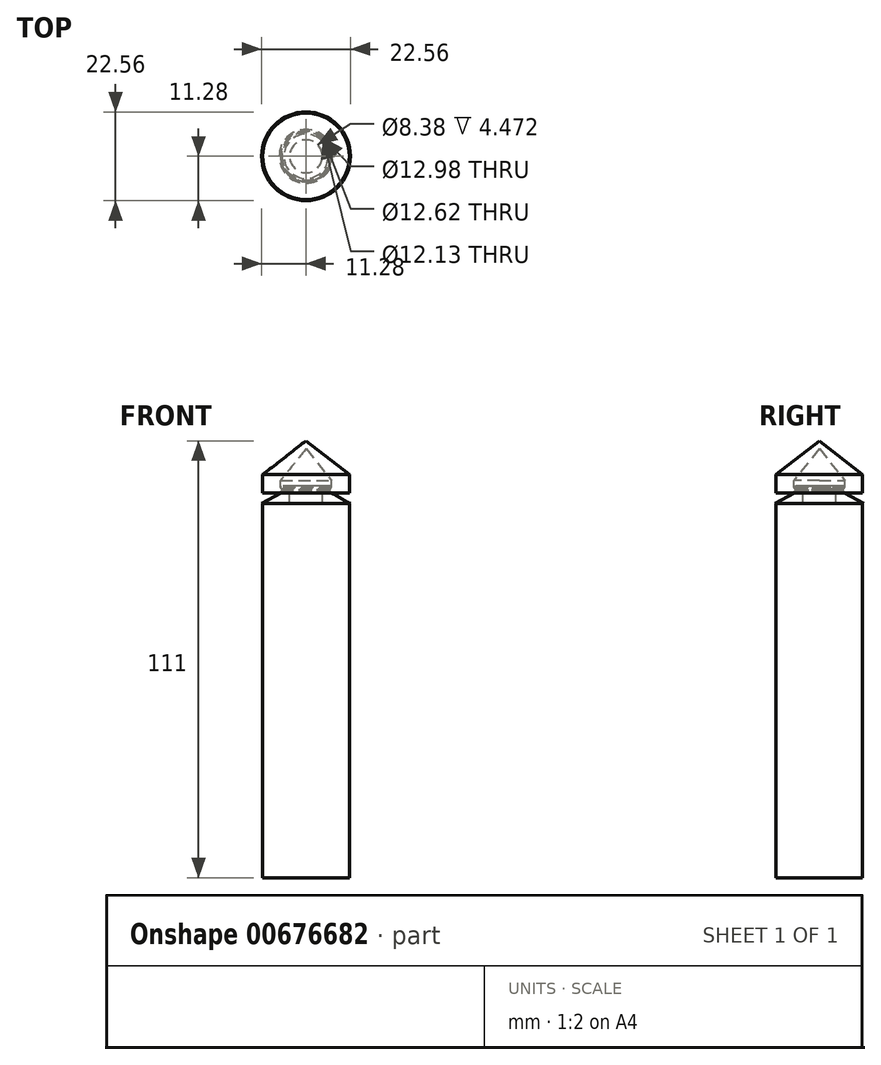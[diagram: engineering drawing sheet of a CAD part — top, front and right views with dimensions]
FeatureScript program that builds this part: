
annotation { "Feature Type Name" : "Feature", "Feature Type Description" : "" }
export const myFeature = defineFeature(function(context is Context, id is Id, definition is map)
    precondition{}
    {
        {
            var Q0;
            Q0=qCreatedBy(makeId("Front.planeOp"),FACE);
            var sketch = newSketch(context, id + "F0", { "sketchPlane" : qUnion([Q0])});
            skLineSegment(sketch, "E0", {"start": v(0, 27.08) * mm, "end": v(0, -28.09) * mm});
            skLineSegment(sketch, "E1", {"start": v(0, 21.5) * mm, "end": v(11, 12.9) * mm});
            skLineSegment(sketch, "E2", {"start": v(6.5, 11.4) * mm, "end": v(0, 19.49) * mm});
            skLineSegment(sketch, "E3", {"start": v(0, -89.5) * mm, "end": v(12.79, -89.5) * mm});
            skLineSegment(sketch, "E4", {"start": v(12.79, -89.5) * mm, "end": v(11, -89.5) * mm});
            skLineSegment(sketch, "E5", {"start": v(11, -89.5) * mm, "end": v(11, 5.52) * mm});
            skLineSegment(sketch, "E6", {"start": v(11.72, 5.52) * mm, "end": v(11, 5.52) * mm});
            skLineSegment(sketch, "E7", {"start": v(6.3, 9.42) * mm, "end": v(6.3, 10) * mm});
            skLineSegment(sketch, "E8", {"start": v(6.3, 10) * mm, "end": v(4.19, 10) * mm});
            skLineSegment(sketch, "E9", {"start": v(4.19, 10) * mm, "end": v(4.19, 5.52) * mm});
            skLineSegment(sketch, "E10", {"start": v(4.19, 5.52) * mm, "end": v(0, 5.52) * mm});
            skLineSegment(sketch, "E11", {"start": v(0, -28.09) * mm, "end": v(0, -89.5) * mm});
            skLineSegment(sketch, "E12", {"start": v(6.5, 11.4) * mm, "end": v(6.5, 9.64) * mm});
            skLineSegment(sketch, "E13", {"start": v(6.5, 9.64) * mm, "end": v(6.06, 9.3) * mm});
            skLineSegment(sketch, "E14", {"start": v(6.06, 8.71) * mm, "end": v(6.82, 8.29) * mm});
            skLineSegment(sketch, "E15", {"start": v(11, 5.52) * mm, "end": v(11.72, 5.52) * mm});
            skLineSegment(sketch, "E16", {"start": v(11, 8.29) * mm, "end": v(11, 12.9) * mm});
            skLineSegment(sketch, "E17", {"start": v(6.82, 8.29) * mm, "end": v(11, 8.29) * mm});
            skLineSegment(sketch, "E18", {"start": v(11.72, 5.52) * mm, "end": v(11.28, 5.52) * mm});
            skLineSegment(sketch, "E19", {"start": v(11.28, 5.52) * mm, "end": v(5.63, 8.7) * mm});
            skLineSegment(sketch, "E20", {"start": v(5.63, 8.7) * mm, "end": v(5.63, 8.95) * mm});
            skLineSegment(sketch, "E21", {"start": v(5.63, 8.95) * mm, "end": v(6.3, 9.42) * mm});
            skLineSegment(sketch, "E22", {"start": v(6.06, 9.3) * mm, "end": v(6.06, 8.71) * mm});
            skPoint(sketch, "E23.orphan", {"position": v(5.63, 8.95) * mm});
            skSolve(sketch);
        }
        {
            var Q0;
            {var subQ0=sQuery(id+"F0.wireOp",EDGE,"E3");Q0=makeQuery(id+"F0.imprint","IMPRINT",FACE,{"disambiguationData":[TD([[makeQuery(id+"F0.imprint","IMPRINT",EDGE,{"derivedFrom":subQ0}),1.0]])]});}
            var Q1;
            {var subQ0=sQuery(id+"F0.wireOp",EDGE,"E1");Q1=makeQuery(id+"F0.imprint","IMPRINT",FACE,{"disambiguationData":[TD([[makeQuery(id+"F0.imprint","IMPRINT",EDGE,{"derivedFrom":subQ0}),-1.0]])]});}
            var Q2;
            Q2=sQuery(id+"F0.wireOp",EDGE,"E0");
            revolve(context, id + "F1", {"entities" : qUnion([Q0, Q1]), "axis" : qUnion([Q2]), "revolveType" : RevolveType.FULL});
        }
    });
